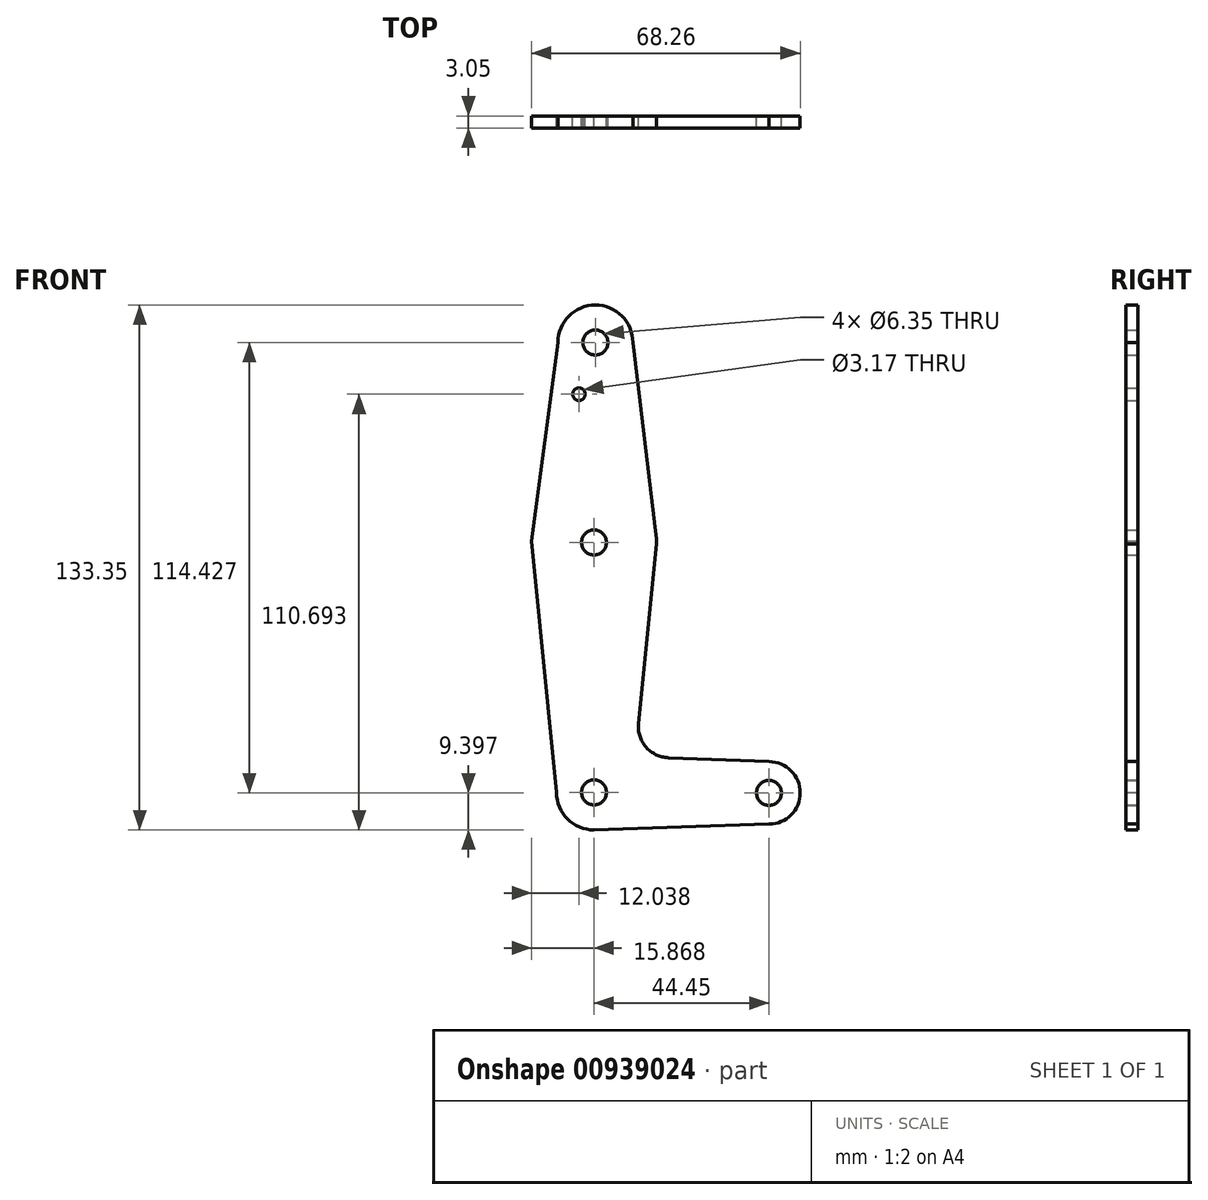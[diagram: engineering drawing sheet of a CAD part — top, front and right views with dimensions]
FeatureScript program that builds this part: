
annotation { "Feature Type Name" : "Feature", "Feature Type Description" : "" }
export const myFeature = defineFeature(function(context is Context, id is Id, definition is map)
    precondition{}
    {
        {
            var Q0;
            Q0=qCreatedBy(makeId("Front.planeOp"),FACE);
            var sketch = newSketch(context, id + "F0", { "sketchPlane" : qUnion([Q0])});
            skCircle(sketch, "E0", {"center": v(-33.04, 56.71) * mm, "radius": 9.53 * mm});
            skCircle(sketch, "E1", {"center": v(-33.38, 5.91) * mm, "radius": 15.88 * mm});
            skCircle(sketch, "E2", {"center": v(-33.38, -57.59) * mm, "radius": 9.53 * mm});
            skLineSegment(sketch, "E3", {"start": v(-33.38, -57.59) * mm, "end": v(11.07, -57.71) * mm, "construction": true});
            skCircle(sketch, "E4", {"center": v(11.07, -57.71) * mm, "radius": 7.94 * mm});
            skLineSegment(sketch, "E5", {"start": v(-33.04, 56.71) * mm, "end": v(-33.38, 5.91) * mm, "construction": true});
            skLineSegment(sketch, "E6", {"start": v(-33.38, 5.91) * mm, "end": v(-33.38, -57.59) * mm, "construction": true});
            skLineSegment(sketch, "E7", {"start": v(-23.51, 56.71) * mm, "end": v(-17.44, 6.28) * mm});
            skLineSegment(sketch, "E8", {"start": v(-42.56, 56.71) * mm, "end": v(-49.25, 6.28) * mm});
            skLineSegment(sketch, "E9", {"start": v(-42.9, -57.59) * mm, "end": v(-49.25, 6.28) * mm});
            skLineSegment(sketch, "E10", {"start": v(-22.1, -40.05) * mm, "end": v(-17.44, 6.28) * mm});
            skLineSegment(sketch, "E11", {"start": v(-33.38, -67.11) * mm, "end": v(11.07, -65.65) * mm});
            skLineSegment(sketch, "E12", {"start": v(-14.49, -48.79) * mm, "end": v(11.07, -49.78) * mm});
            skCircle(sketch, "E13", {"center": v(-33.04, 56.71) * mm, "radius": 3.18 * mm});
            skCircle(sketch, "E14", {"center": v(-33.38, 5.91) * mm, "radius": 3.18 * mm});
            skCircle(sketch, "E15", {"center": v(-33.38, -57.59) * mm, "radius": 3.18 * mm});
            skCircle(sketch, "E16", {"center": v(11.07, -57.71) * mm, "radius": 3.18 * mm});
            skCircle(sketch, "E17", {"center": v(-37.21, 43.58) * mm, "radius": 1.59 * mm});
            skArc(sketch, "E18.filletArc", {"start": v(-22.1, -40.05) * mm, "mid": v(-20.18, -46.06) * mm, "end": v(-14.49, -48.79) * mm});
            skSolve(sketch);
        }
        {
            var Q0;
            Q0=makeQuery(id+"F0.imprint","IMPRINT",FACE,{"disambiguationData":[TD([[makeQuery(id+"F0.imprint","IMPRINT",EDGE,{"derivedFrom":sQuery(id+"F0.wireOp",EDGE,"E13")}),-1.0]])]});
            var Q1;
            Q1=makeQuery(id+"F0.imprint","IMPRINT",FACE,{"disambiguationData":[TD([[makeQuery(id+"F0.imprint","IMPRINT",EDGE,{"derivedFrom":sQuery(id+"F0.wireOp",EDGE,"E17")}),-1.0]])]});
            var Q2;
            Q2=makeQuery(id+"F0.imprint","IMPRINT",FACE,{"disambiguationData":[TD([[makeQuery(id+"F0.imprint","IMPRINT",EDGE,{"derivedFrom":sQuery(id+"F0.wireOp",EDGE,"E14")}),-1.0]])]});
            var Q3;
            {var subQ8=sQuery(id+"F0.wireOp",EDGE,"E12");Q3=makeQuery(id+"F0.imprint","IMPRINT",FACE,{"disambiguationData":[TD([[makeQuery(id+"F0.imprint","IMPRINT",EDGE,{"derivedFrom":subQ8}),-1.0]])]});}
            var Q4;
            Q4=makeQuery(id+"F0.imprint","IMPRINT",FACE,{"disambiguationData":[TD([[makeQuery(id+"F0.imprint","IMPRINT",EDGE,{"derivedFrom":sQuery(id+"F0.wireOp",EDGE,"E15")}),-1.0]])]});
            var Q5;
            Q5=makeQuery(id+"F0.imprint","IMPRINT",FACE,{"disambiguationData":[TD([[makeQuery(id+"F0.imprint","IMPRINT",EDGE,{"derivedFrom":sQuery(id+"F0.wireOp",EDGE,"E16")}),-1.0]])]});
            extrude(context, id + "F1", {"entities" : qUnion([Q0, Q1, Q2, Q3, Q4, Q5]), "depth" : 3.05 * mm, "offsetDistance" : 25.4 * mm});
        }
    });
